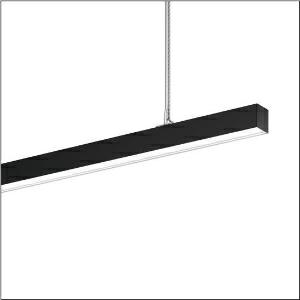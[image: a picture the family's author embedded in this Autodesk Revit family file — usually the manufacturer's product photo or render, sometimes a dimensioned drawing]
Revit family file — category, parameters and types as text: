
# Revit family: silica_r__21_51mx33da37bb_2abf
name_source: partatom
category: Lighting Fixtures
units: mm (PartAtom-declared; Revit-internal decimal feet)

## family parameters
Cut with Voids When Loaded = No
Host = Face
Light Source = No
Part Type = Normal
Room Calculation Point = No
Round Connector Dimension = Use Diameter
Shared = No

## types (1)
- --- (1 x LED, 5910 lm, 41.3 W, 3000K)
    Apparent Load = 41 VA
    CIE Flux Codes = 78 96 99 55 100
    Color Rendering = 80
    Color Temperature = 3000K
    Default Elevation = 1800 mm
    Description = Silica® 21, office luminaire, primary optical cover: prismatic diffuser, of PMMA, CAT 2 (L<= 3000cd/m²), light emission: direct/indirect distribution, primary light characteristic: symmetric, installation type: suspended mounting, LED, rated luminous flux: 5.910lm, luminous efficacy: 143lm/W, light colour: 830, colour temperature: 3000K, with terminal, 3+2-pole, max. 2.5mm², mains connection: 220..240V, AC, 50/60Hz, rated input power: 41.3W, luminaire housing, of aluminium, jet black (RAL 9005), length: 1.204mm, width: 53mm, height: 53mm, protection rating (complete): IP20, insulation class (complete): insulation class I (protective earthing), certification: CE, permissible operating ambient temperature: 0..+35°C, standard: EN 50419, packaging unit: 1 piece
    Height = 53 mm
    Lamp = 1 x LED
    Lamp Light Flux = 5910 lm
    Lamp Power = 41.3 W
    Lamp count = 1
    Length = 1204 mm
    Luminous efficacy = 143 lm/W
    Manufacturer = Siteco
    ModVariant = No
    Model = 51MX33DA37BB
    Mounting Place = Ceiling
    Mounting Type = Pendant
    Number of Poles = 1
    OnlyDefault = Yes
    Power Factor = 1
    Product Name = Silica® 21
    Product group = office luminaire | ceiling pendant
    ProductGroupID = 902
    Protection Class = Protection class I
    Protection Degree = IP 20
    RLX_Detail_Level = 1
    RLX_Emergency_Light_Flux = 0 lm
    RLX_Emergency_Type = 0
    RLX_Emergency_Type_DB = No
    RlxData = <blob elided: 26101 chars, md5=dd056686>
    Socket = socket
    Standby Power = 0 W
    System Light Flux = 5910 lm
    System Power = 41 W
    Type Comments = factory setting: luminous flux: 100 % | dim-lin: 254 | 345 mA
    Type Image = l_1313646.jpg
    URL = http://relux.com
    VarID = @adj_067229
    Voltage = 0 V
    Weight = 0.00 kg
    Width = 53 mm

## geometry (parser evidence)
native form markers: Blend x4, Sweep x14
no freeform markers — native parametric forms only
